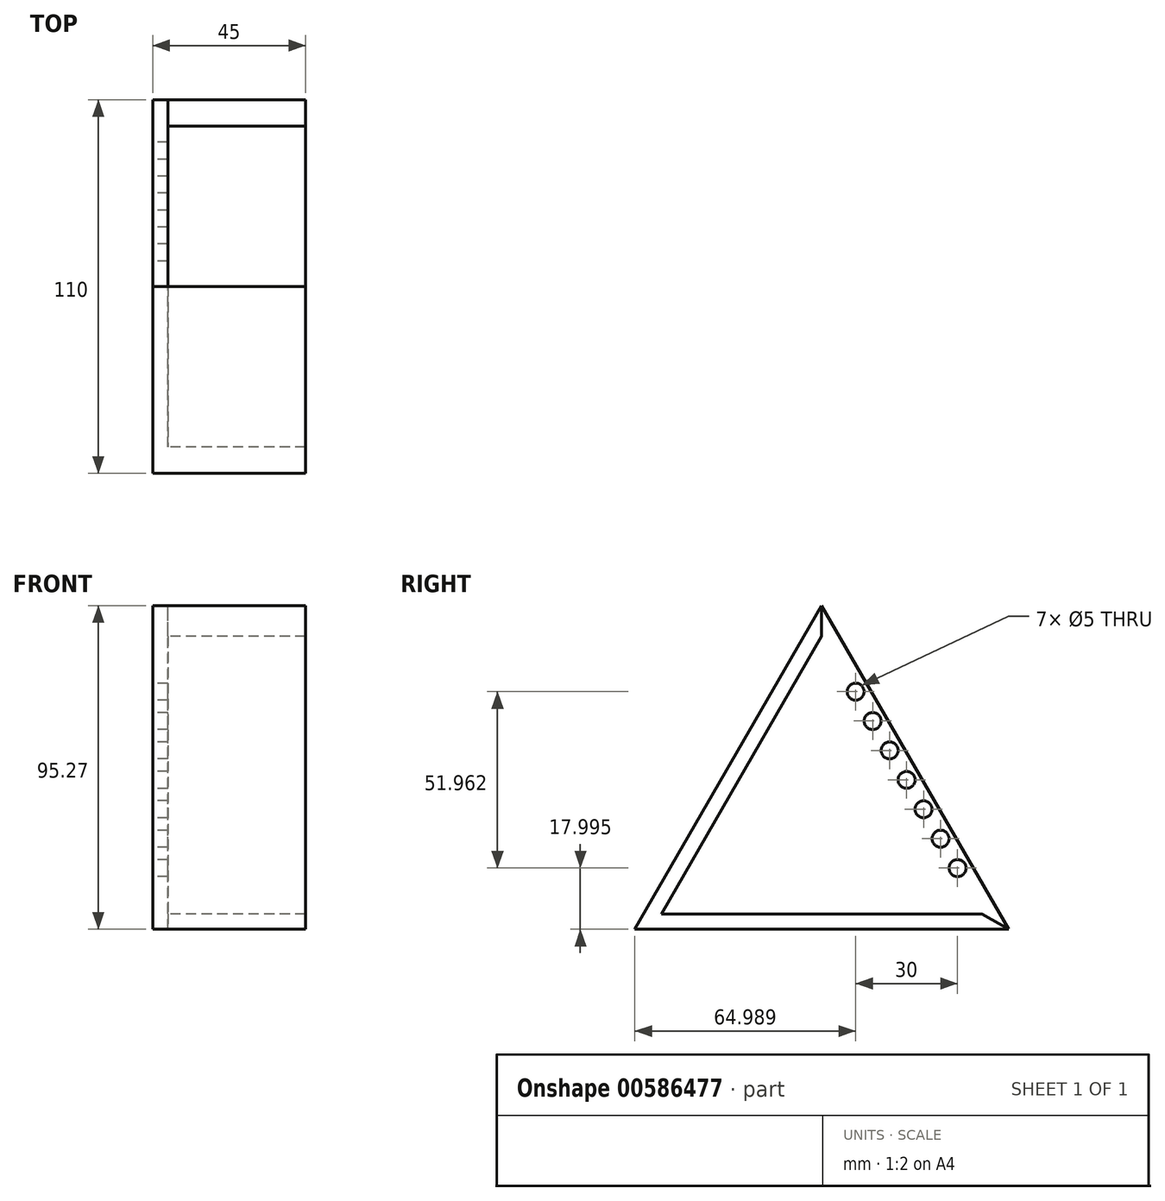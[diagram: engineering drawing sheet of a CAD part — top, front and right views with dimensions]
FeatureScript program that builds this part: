
annotation { "Feature Type Name" : "Feature", "Feature Type Description" : "" }
export const myFeature = defineFeature(function(context is Context, id is Id, definition is map)
    precondition{}
    {
        {
            var Q0;
            Q0=qCreatedBy(makeId("Right.planeOp"),FACE);
            var sketch = newSketch(context, id + "F0", { "sketchPlane" : qUnion([Q0])});
            skLineSegment(sketch, "E0", {"start": v(-101.73, -11.14) * mm, "end": v(8.27, -11.14) * mm});
            skLineSegment(sketch, "E1", {"start": v(-46.73, -11.14) * mm, "end": v(-46.73, 74.95) * mm, "construction": true});
            skLineSegment(sketch, "E2", {"start": v(8.27, -11.14) * mm, "end": v(-46.73, 84.13) * mm});
            skLineSegment(sketch, "E3", {"start": v(-46.73, 84.13) * mm, "end": v(-101.73, -11.14) * mm});
            skSolve(sketch);
        }
        {
            var Q0;
            Q0=makeQuery(id+"F0.imprint","IMPRINT",FACE,{"disambiguationData":[TD([[makeQuery(id+"F0.imprint","IMPRINT",EDGE,{"derivedFrom":sQuery(id+"F0.wireOp",EDGE,"E0")}),1.0]])]});
            extrude(context, id + "F1", {"entities" : qUnion([Q0]), "depth" : 45 * mm, "offsetDistance" : 25 * mm});
        }
        {
            var Q0;
            Q0=makeQuery(id+"F1.opExtrude","CAP_FACE",FACE,{"disambiguationData":[OSD([sQuery(id+"F0.wireOp",EDGE,"E0"),sQuery(id+"F0.wireOp",EDGE,"E2"),sQuery(id+"F0.wireOp",EDGE,"E3")])],"isStart":false});
            shell(context, id + "F2", {"entities" : qUnion([Q0]), "thickness" : 4.5 * mm});
        }
        {
            var Q0;
            Q0=makeQuery(id+"F1.opExtrude","CAP_FACE",FACE,{"disambiguationData":[OSD([sQuery(id+"F0.wireOp",EDGE,"E0"),sQuery(id+"F0.wireOp",EDGE,"E2"),sQuery(id+"F0.wireOp",EDGE,"E3")])],"isStart":true});
            var sketch = newSketch(context, id + "F3", { "sketchPlane" : qUnion([Q0])});
            skCircle(sketch, "E4", {"center": v(6.74, 6.86) * mm, "radius": 2 * mm});
            skLineSegment(sketch, "E5", {"start": v(6.74, 6.86) * mm, "end": v(3.28, 8.86) * mm});
            skLineSegment(sketch, "E6", {"start": v(6.74, 6.86) * mm, "end": v(-2, -11.14) * mm});
            skLineSegment(sketch, "E7", {"start": v(6.74, 6.86) * mm, "end": v(11.74, 15.52) * mm});
            skCircle(sketch, "E8.1.0.0", {"center": v(11.74, 15.52) * mm, "radius": 2 * mm});
            skCircle(sketch, "E8.2.0.0", {"center": v(16.74, 24.18) * mm, "radius": 2 * mm});
            skCircle(sketch, "E8.3.0.0", {"center": v(21.74, 32.84) * mm, "radius": 2 * mm});
            skCircle(sketch, "E8.4.0.0", {"center": v(26.74, 41.5) * mm, "radius": 2 * mm});
            skCircle(sketch, "E8.5.0.0", {"center": v(31.74, 50.16) * mm, "radius": 2 * mm});
            skCircle(sketch, "E8.6.0.0", {"center": v(36.74, 58.82) * mm, "radius": 2 * mm});
            skLineSegment(sketch, "E8.direction1", {"start": v(6.74, 6.86) * mm, "end": v(11.74, 15.52) * mm, "construction": true});
            skSolve(sketch);
        }
        {
            var Q0;
            Q0=sQuery(id+"F3.wireOp",VERTEX,"E8.6.0.0.center");
            var Q1;
            Q1=sQuery(id+"F3.wireOp",VERTEX,"E8.5.0.0.center");
            var Q2;
            Q2=sQuery(id+"F3.wireOp",VERTEX,"E8.4.0.0.center");
            var Q3;
            Q3=sQuery(id+"F3.wireOp",VERTEX,"E8.3.0.0.center");
            var Q4;
            Q4=sQuery(id+"F3.wireOp",VERTEX,"E8.2.0.0.center");
            var Q5;
            Q5=sQuery(id+"F3.wireOp",VERTEX,"E7.end");
            var Q6;
            Q6=sQuery(id+"F3.wireOp",VERTEX,"E5.start");
            var Q7;
            Q7=makeQuery(id+"F1.opExtrude","SWEPT_BODY",BODY,{"disambiguationData":[OSD([sQuery(id+"F0.wireOp",EDGE,"E0"),sQuery(id+"F0.wireOp",EDGE,"E2"),sQuery(id+"F0.wireOp",EDGE,"E3")])]});
            hole(context, id + "F4", {"style" : HoleStyle.SIMPLE, "endStyle" : HoleEndStyle.BLIND, "holeDiameter" : 5 * mm, "majorDiameter" : 5 * mm, "holeDepth" : 12 * mm, "isTappedThrough" : true, "tappedDepth" : 12 * mm, "tapClearance" : 3, "locations" : qUnion([Q0, Q1, Q2, Q3, Q4, Q5, Q6]), "scope" : qUnion([Q7])});
        }
        {
            var Q0;
            Q0=makeQuery(id+"F1.opExtrude","CAP_FACE",FACE,{"disambiguationData":[OSD([sQuery(id+"F0.wireOp",EDGE,"E0"),sQuery(id+"F0.wireOp",EDGE,"E2"),sQuery(id+"F0.wireOp",EDGE,"E3")])],"isStart":false});
            var sketch = newSketch(context, id + "F5", { "sketchPlane" : qUnion([Q0])});
            skLineSegment(sketch, "E9", {"start": v(-46.73, 75.13) * mm, "end": v(-46.73, 84.13) * mm});
            skLineSegment(sketch, "E10", {"start": v(0.47, -6.64) * mm, "end": v(8.27, -11.14) * mm});
            skSolve(sketch);
        }
        {
            var Q0;
            Q0=makeQuery(id+"F5.imprint","IMPRINT",FACE,{"disambiguationData":[TD([[makeQuery(id+"F5.imprint","IMPRINT",EDGE,{"derivedFrom":sQuery(id+"F5.wireOp",EDGE,"E9")}),-1.0]])]});
            extrude(context, id + "F6", {"entities" : qUnion([Q0]), "operationType" : NewBodyOperationType.REMOVE, "endBound" : BoundingType.SYMMETRIC, "oppositeDirection" : true, "depth" : 81 * mm, "offsetDistance" : 25 * mm});
        }
    });
